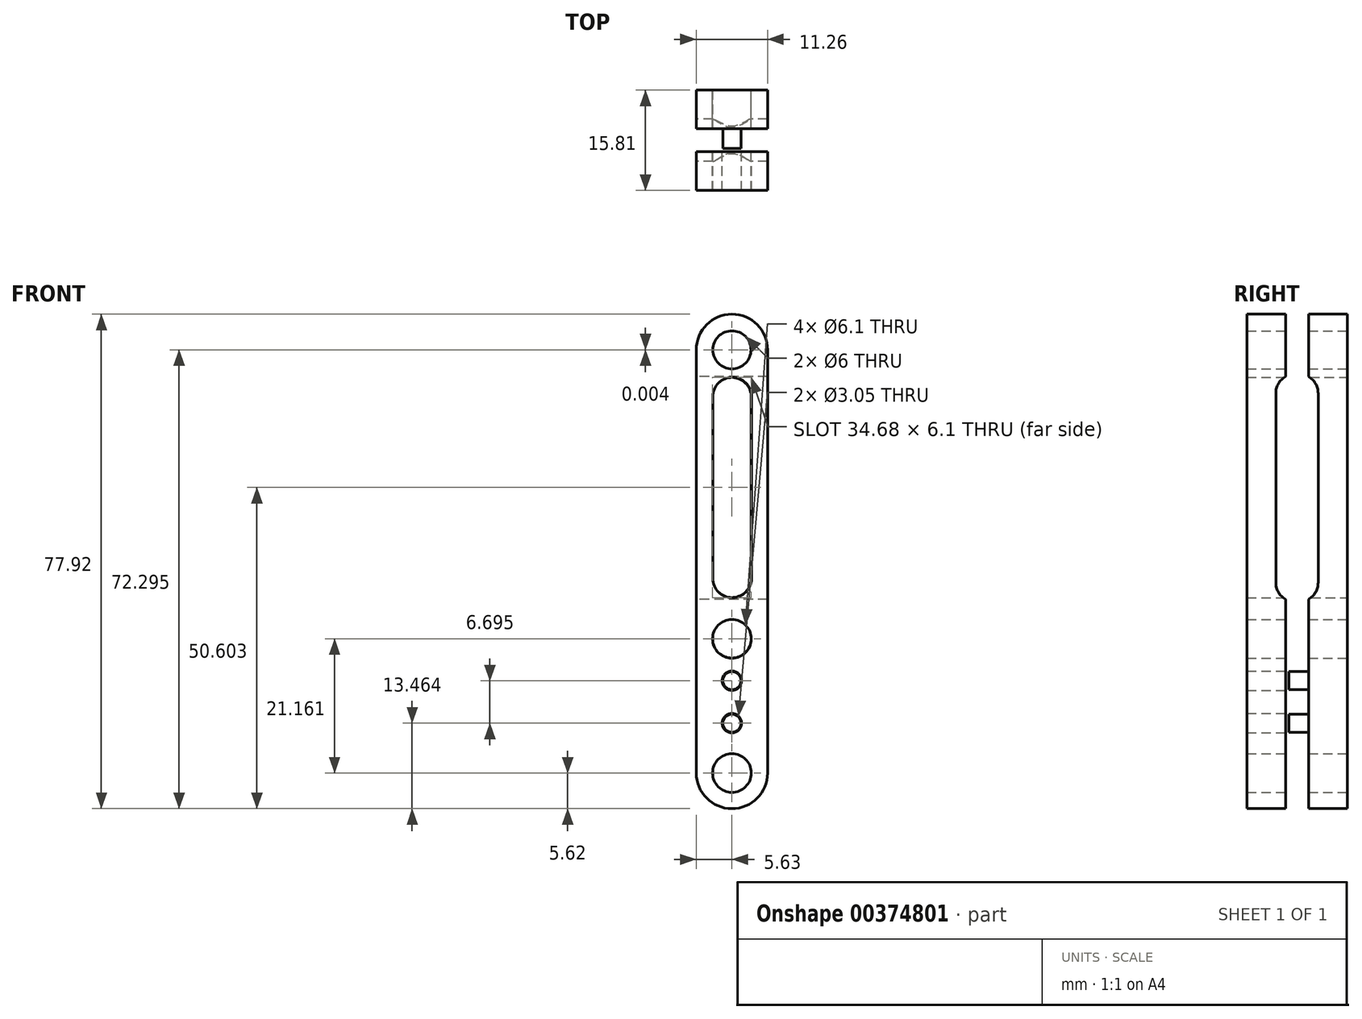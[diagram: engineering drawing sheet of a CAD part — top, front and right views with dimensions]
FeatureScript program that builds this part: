
annotation { "Feature Type Name" : "Feature", "Feature Type Description" : "" }
export const myFeature = defineFeature(function(context is Context, id is Id, definition is map)
    precondition{}
    {
        {
            var Q0;
            Q0=qCreatedBy(makeId("Front.planeOp"),FACE);
            var sketch = newSketch(context, id + "F0", { "sketchPlane" : qUnion([Q0])});
            skLineSegment(sketch, "E0", {"start": v(-0.75, 8.9) * mm, "end": v(-0.75, 0) * mm});
            skLineSegment(sketch, "E1", {"start": v(0.75, 0) * mm, "end": v(0.75, 8.9) * mm});
            skArc(sketch, "E2", {"start": v(-0.75, 8.9) * mm, "mid": v(0, 9.64) * mm, "end": v(0.75, 8.9) * mm});
            skArc(sketch, "E3", {"start": v(0.75, 0) * mm, "mid": v(0, -0.75) * mm, "end": v(-0.75, 0) * mm});
            skPoint(sketch, "E4.centerSnap0", {"position": v(0, 7.9) * mm});
            skCircle(sketch, "E5", {"center": v(0, 2.82) * mm, "radius": 0.4 * mm});
            skPoint(sketch, "E5.centerSnap0", {"position": v(0, 4.09) * mm});
            skCircle(sketch, "E6", {"center": v(0, 0) * mm, "radius": 0.4 * mm});
            skCircle(sketch, "E7", {"center": v(0, 8.9) * mm, "radius": 0.4 * mm});
            skArc(sketch, "E8", {"start": v(0.41, 7.9) * mm, "mid": v(0, 8.32) * mm, "end": v(-0.4, 7.9) * mm});
            skArc(sketch, "E9", {"start": v(-0.4, 4.09) * mm, "mid": v(0, 3.68) * mm, "end": v(0.41, 4.09) * mm});
            skLineSegment(sketch, "E10", {"start": v(-0.4, 7.9) * mm, "end": v(-0.4, 4.09) * mm});
            skLineSegment(sketch, "E11", {"start": v(0.41, 7.9) * mm, "end": v(0.41, 4.09) * mm});
            skCircle(sketch, "E12", {"center": v(0, 1.05) * mm, "radius": 0.2 * mm});
            skPoint(sketch, "E13.centerSnap0", {"position": v(0, 9.64) * mm});
            skCircle(sketch, "E14", {"center": v(0, 1.94) * mm, "radius": 0.2 * mm});
            skSolve(sketch);
        }
        {
            var Q0;
            Q0=makeQuery(id+"F0.imprint","IMPRINT",FACE,{"disambiguationData":[TD([[makeQuery(id+"F0.imprint","IMPRINT",EDGE,{"derivedFrom":sQuery(id+"F0.wireOp",EDGE,"E0")}),1.0]])]});
            extrude(context, id + "F1", {"entities" : qUnion([Q0]), "endBound" : BoundingType.SYMMETRIC, "depth" : 0.81 * mm, "offsetDistance" : 25.4 * mm});
        }
        {
            var Q0;
            Q0=qCreatedBy(makeId("Right.planeOp"),FACE);
            cPlane(context, id + "F2", {"entities" : qUnion([Q0]), "cplaneType" : CPlaneType.OFFSET, "offset" : 7.87 * mm, "oppositeDirection" : true, "width" : 152.4 * mm, "height" : 152.4 * mm});
        }
        {
            var Q0;
            Q0=makeQuery(id+"F1.opExtrude","CAP_FACE",FACE,{"disambiguationData":[OSD([sQuery(id+"F0.wireOp",EDGE,"E0"),sQuery(id+"F0.wireOp",EDGE,"E1"),sQuery(id+"F0.wireOp",EDGE,"E2"),sQuery(id+"F0.wireOp",EDGE,"E3"),sQuery(id+"F0.wireOp",EDGE,"E5"),sQuery(id+"F0.wireOp",EDGE,"E6"),sQuery(id+"F0.wireOp",EDGE,"E7"),sQuery(id+"F0.wireOp",EDGE,"E8"),sQuery(id+"F0.wireOp",EDGE,"E9"),sQuery(id+"F0.wireOp",EDGE,"E10"),sQuery(id+"F0.wireOp",EDGE,"E11")])],"isStart":true});
            cPlane(context, id + "F3", {"entities" : qUnion([Q0]), "cplaneType" : CPlaneType.OFFSET, "offset" : 0.89 * mm, "width" : 152.4 * mm, "height" : 152.4 * mm});
        }
        {
            var Q0;
            Q0=qCreatedBy(id+"F3.planeOp",FACE);
            var sketch = newSketch(context, id + "F4", { "sketchPlane" : qUnion([Q0])});
            skLineSegment(sketch, "E15", {"start": v(-0.75, 8.9) * mm, "end": v(-0.75, 0) * mm});
            skLineSegment(sketch, "E16", {"start": v(0.75, 0) * mm, "end": v(0.75, 8.9) * mm});
            skArc(sketch, "E17", {"start": v(-0.75, 8.9) * mm, "mid": v(0, 9.64) * mm, "end": v(0.75, 8.9) * mm});
            skArc(sketch, "E18", {"start": v(0.75, 0) * mm, "mid": v(0, -0.75) * mm, "end": v(-0.75, 0) * mm});
            skPoint(sketch, "E19.centerSnap0", {"position": v(0, 7.9) * mm});
            skCircle(sketch, "E20", {"center": v(0, 2.82) * mm, "radius": 0.4 * mm});
            skPoint(sketch, "E20.centerSnap0", {"position": v(0, 4.1) * mm});
            skCircle(sketch, "E21", {"center": v(0, 0) * mm, "radius": 0.4 * mm});
            skCircle(sketch, "E22", {"center": v(0, 8.9) * mm, "radius": 0.4 * mm});
            skArc(sketch, "E23", {"start": v(0.4, 7.9) * mm, "mid": v(0, 8.3) * mm, "end": v(-0.4, 7.9) * mm});
            skArc(sketch, "E24", {"start": v(-0.4, 4.1) * mm, "mid": v(0, 3.69) * mm, "end": v(0.4, 4.1) * mm});
            skLineSegment(sketch, "E25", {"start": v(-0.4, 7.9) * mm, "end": v(-0.4, 4.1) * mm});
            skLineSegment(sketch, "E26", {"start": v(0.4, 7.9) * mm, "end": v(0.4, 4.1) * mm});
            skCircle(sketch, "E27", {"center": v(0, 1.05) * mm, "radius": 0.2 * mm});
            skCircle(sketch, "E28", {"center": v(0, 1.94) * mm, "radius": 0.2 * mm});
            skPoint(sketch, "E29.center.orphan", {"position": v(0, 9.46) * mm});
            skSolve(sketch);
        }
        {
            var Q0;
            Q0=makeQuery(id+"F1.opExtrude","CAP_FACE",FACE,{"disambiguationData":[OSD([sQuery(id+"F0.wireOp",EDGE,"E0"),sQuery(id+"F0.wireOp",EDGE,"E1"),sQuery(id+"F0.wireOp",EDGE,"E2"),sQuery(id+"F0.wireOp",EDGE,"E3"),sQuery(id+"F0.wireOp",EDGE,"E5"),sQuery(id+"F0.wireOp",EDGE,"E6"),sQuery(id+"F0.wireOp",EDGE,"E7"),sQuery(id+"F0.wireOp",EDGE,"E8"),sQuery(id+"F0.wireOp",EDGE,"E9"),sQuery(id+"F0.wireOp",EDGE,"E10"),sQuery(id+"F0.wireOp",EDGE,"E11")])],"isStart":true});
            cPlane(context, id + "F5", {"entities" : qUnion([Q0]), "cplaneType" : CPlaneType.OFFSET, "offset" : 1.63 * mm, "width" : 152.4 * mm, "height" : 152.4 * mm});
        }
        {
            var Q0;
            Q0=makeQuery(id+"F4.imprint","IMPRINT",FACE,{"disambiguationData":[TD([[makeQuery(id+"F4.imprint","IMPRINT",EDGE,{"derivedFrom":sQuery(id+"F4.wireOp",EDGE,"E15")}),1.0]])]});
            var Q1;
            Q1=makeQuery(id+"F4.imprint","IMPRINT",FACE,{"disambiguationData":[TD([[makeQuery(id+"F4.imprint","IMPRINT",EDGE,{"derivedFrom":sQuery(id+"F4.wireOp",EDGE,"E27")}),1.0]])]});
            var Q2;
            Q2=makeQuery(id+"F4.imprint","IMPRINT",FACE,{"disambiguationData":[TD([[makeQuery(id+"F4.imprint","IMPRINT",EDGE,{"derivedFrom":sQuery(id+"F4.wireOp",EDGE,"E28")}),1.0]])]});
            extrude(context, id + "F6", {"entities" : qUnion([Q0, Q1, Q2]), "endBound" : BoundingType.SYMMETRIC, "oppositeDirection" : true, "depth" : 0.81 * mm, "offsetDistance" : 25.4 * mm});
        }
        {
            var Q0;
            Q0=makeQuery(id+"F4.imprint","IMPRINT",FACE,{"disambiguationData":[TD([[makeQuery(id+"F4.imprint","IMPRINT",EDGE,{"derivedFrom":sQuery(id+"F4.wireOp",EDGE,"E27")}),1.0]])]});
            var Q1;
            Q1=makeQuery(id+"F4.imprint","IMPRINT",FACE,{"disambiguationData":[TD([[makeQuery(id+"F4.imprint","IMPRINT",EDGE,{"derivedFrom":sQuery(id+"F4.wireOp",EDGE,"E28")}),1.0]])]});
            extrude(context, id + "F7", {"entities" : qUnion([Q0, Q1]), "operationType" : NewBodyOperationType.ADD, "oppositeDirection" : true, "depth" : 0.82 * mm, "offsetDistance" : 25.4 * mm});
        }
        {
            var Q0;
            Q0=qCreatedBy(id+"F2.planeOp",FACE);
            var sketch = newSketch(context, id + "F8", { "sketchPlane" : qUnion([Q0])});
            skLineSegment(sketch, "E30", {"start": v(5.25, 8.38) * mm, "end": v(-1.98, 8.38) * mm, "construction": true});
            skLineSegment(sketch, "E31", {"start": v(5.33, 3.6) * mm, "end": v(-2.3, 3.6) * mm, "construction": true});
            skLineSegment(sketch, "E32", {"start": v(5.3, 7.98) * mm, "end": v(-2.02, 7.98) * mm, "construction": true});
            skLineSegment(sketch, "E33", {"start": v(5.35, 4) * mm, "end": v(-2.25, 4) * mm, "construction": true});
            skLineSegment(sketch, "E34", {"start": v(1.1, 7.98) * mm, "end": v(1.1, 4) * mm});
            skLineSegment(sketch, "E35", {"start": v(0.2, 7.98) * mm, "end": v(0.2, 4) * mm});
            skPoint(sketch, "E36", {"position": v(1.1, 4) * mm});
            skPoint(sketch, "E37", {"position": v(1.1, 3.6) * mm});
            skPoint(sketch, "E38", {"position": v(0.2, 3.6) * mm});
            skPoint(sketch, "E39", {"position": v(0.2, 4) * mm});
            skPoint(sketch, "E40", {"position": v(0.2, 8.38) * mm});
            skPoint(sketch, "E41", {"position": v(0.2, 7.98) * mm});
            skPoint(sketch, "E42", {"position": v(1.1, 8.38) * mm});
            skPoint(sketch, "E43", {"position": v(1.1, 7.98) * mm});
            skArc(sketch, "E44", {"start": v(1.1, 7.98) * mm, "mid": v(0.97, 8.26) * mm, "end": v(0.69, 8.38) * mm});
            skArc(sketch, "E45", {"start": v(0.2, 7.98) * mm, "mid": v(0.32, 8.26) * mm, "end": v(0.6, 8.38) * mm});
            skArc(sketch, "E46", {"start": v(1.1, 4) * mm, "mid": v(0.97, 3.71) * mm, "end": v(0.69, 3.6) * mm});
            skArc(sketch, "E47", {"start": v(0.2, 4) * mm, "mid": v(0.32, 3.72) * mm, "end": v(0.6, 3.6) * mm});
            skLineSegment(sketch, "E48", {"start": v(0.69, 8.38) * mm, "end": v(0.69, 3.6) * mm});
            skLineSegment(sketch, "E49", {"start": v(0.6, 8.38) * mm, "end": v(0.6, 3.6) * mm});
            skSolve(sketch);
        }
        {
            var Q0;
            Q0=makeQuery(id+"F8.imprint","IMPRINT",FACE,{"disambiguationData":[TD([[makeQuery(id+"F8.imprint","IMPRINT",EDGE,{"derivedFrom":sQuery(id+"F8.wireOp",EDGE,"E34")}),-1.0]])]});
            extrude(context, id + "F9", {"entities" : qUnion([Q0]), "operationType" : NewBodyOperationType.REMOVE, "depth" : 12.7 * mm, "offsetDistance" : 25.4 * mm});
        }
        {
            var Q0;
            Q0=makeQuery(id+"F8.imprint","IMPRINT",FACE,{"disambiguationData":[TD([[makeQuery(id+"F8.imprint","IMPRINT",EDGE,{"derivedFrom":sQuery(id+"F8.wireOp",EDGE,"E35")}),1.0]])]});
            extrude(context, id + "F10", {"entities" : qUnion([Q0]), "operationType" : NewBodyOperationType.REMOVE, "depth" : 11.13 * mm, "offsetDistance" : 25.4 * mm});
        }
        {
            var Q0;
            Q0=makeQuery(id+"F1.opExtrude","SWEPT_BODY",BODY,{"disambiguationData":[OSD([sQuery(id+"F0.wireOp",EDGE,"E0"),sQuery(id+"F0.wireOp",EDGE,"E1"),sQuery(id+"F0.wireOp",EDGE,"E2"),sQuery(id+"F0.wireOp",EDGE,"E3"),sQuery(id+"F0.wireOp",EDGE,"E5"),sQuery(id+"F0.wireOp",EDGE,"E6"),sQuery(id+"F0.wireOp",EDGE,"E7"),sQuery(id+"F0.wireOp",EDGE,"E8"),sQuery(id+"F0.wireOp",EDGE,"E9"),sQuery(id+"F0.wireOp",EDGE,"E10"),sQuery(id+"F0.wireOp",EDGE,"E11"),sQuery(id+"F0.wireOp",EDGE,"E12"),sQuery(id+"F0.wireOp",EDGE,"E13")])]});
            var Q1;
            Q1=makeQuery(id+"F6.opExtrude","SWEPT_BODY",BODY,{"disambiguationData":[OSD([sQuery(id+"F4.wireOp",EDGE,"E15"),sQuery(id+"F4.wireOp",EDGE,"E16"),sQuery(id+"F4.wireOp",EDGE,"E17"),sQuery(id+"F4.wireOp",EDGE,"E18"),sQuery(id+"F4.wireOp",EDGE,"E20"),sQuery(id+"F4.wireOp",EDGE,"E21"),sQuery(id+"F4.wireOp",EDGE,"E22"),sQuery(id+"F4.wireOp",EDGE,"E23"),sQuery(id+"F4.wireOp",EDGE,"E24"),sQuery(id+"F4.wireOp",EDGE,"E25"),sQuery(id+"F4.wireOp",EDGE,"E26"),sQuery(id+"F4.wireOp",EDGE,"E27"),sQuery(id+"F4.wireOp",EDGE,"E29")])]});
            var Q2;
            Q2=qCreatedBy(makeId("Origin.pointOp"),VERTEX);
            transform(context, id + "F11", {"entities" : qUnion([Q0, Q1]), "transformType" : TransformType.SCALE_UNIFORMLY, "scale" : 7.5, "scalePoint" : qUnion([Q2]), "makeCopy" : false});
        }
    });
